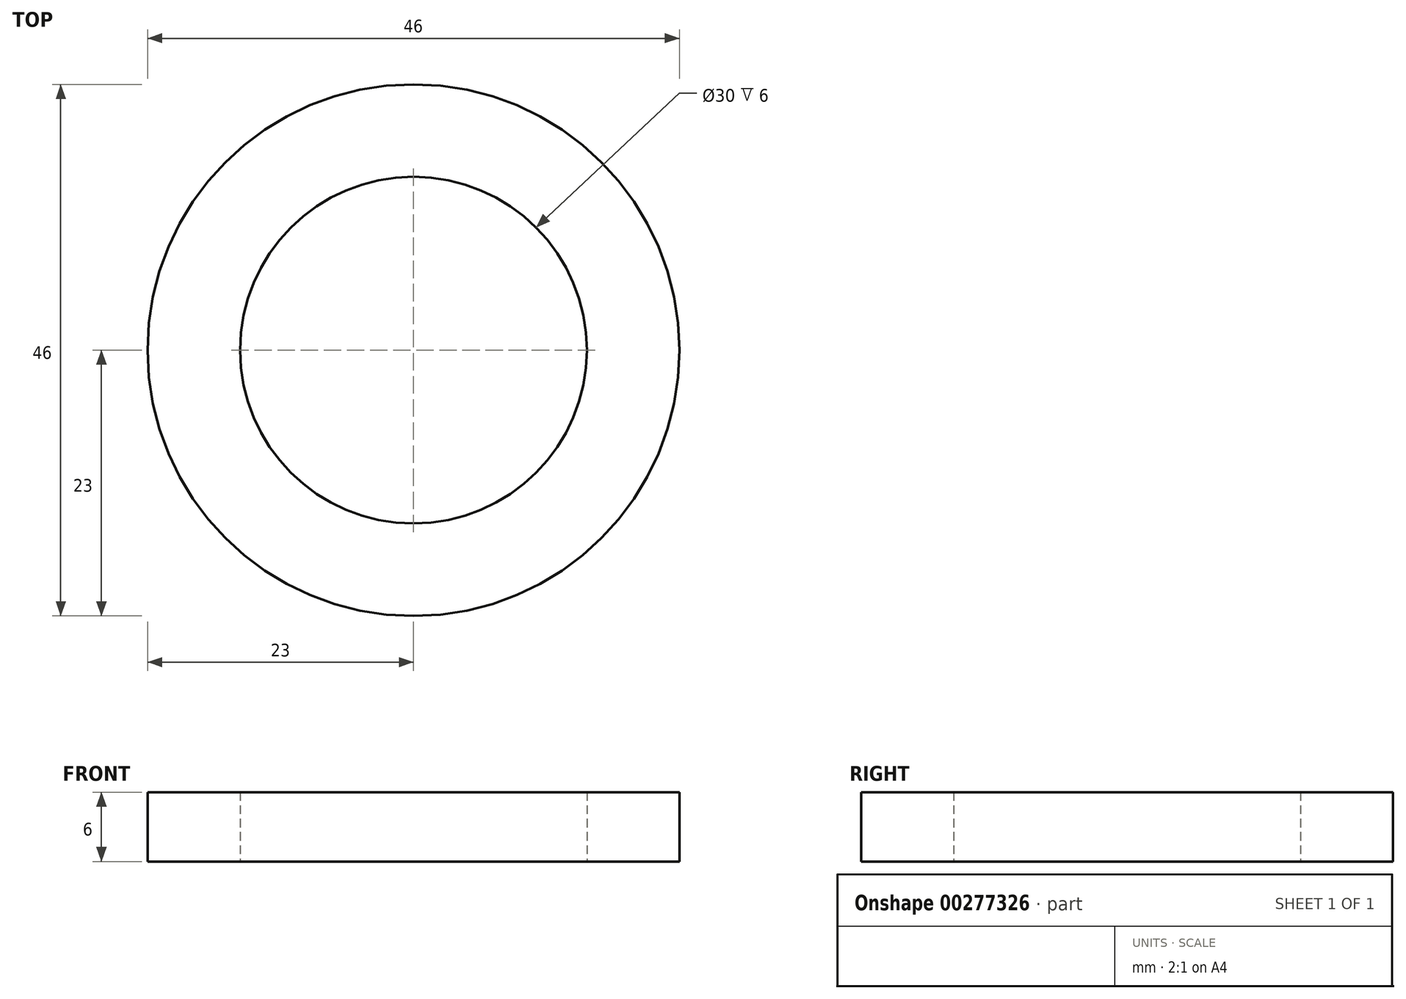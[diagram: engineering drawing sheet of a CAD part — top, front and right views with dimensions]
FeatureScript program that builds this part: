
annotation { "Feature Type Name" : "Feature", "Feature Type Description" : "" }
export const myFeature = defineFeature(function(context is Context, id is Id, definition is map)
    precondition{}
    {
        {
            var Q0;
            Q0=qCreatedBy(makeId("Top.planeOp"),FACE);
            var sketch = newSketch(context, id + "F0", { "sketchPlane" : qUnion([Q0])});
            skCircle(sketch, "E0", {"center": v(0, 0) * mm, "radius": 23 * mm});
            skCircle(sketch, "E1", {"center": v(0, 0) * mm, "radius": 15 * mm});
            skSolve(sketch);
        }
        {
            var Q0;
            Q0 = qSketchRegion(id + "F0", true);
            extrude(context, id + "F1", {"entities" : qUnion([Q0]), "depth" : 6 * mm});
        }
    });
